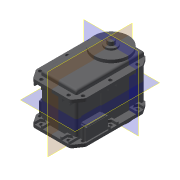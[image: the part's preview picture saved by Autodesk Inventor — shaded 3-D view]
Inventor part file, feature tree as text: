
AUTODESK INVENTOR PART (.ipt)
format: ipt  version: 2020 (Build 240168000, 168)  size: 629,248 bytes
history: native  units: mm
features: other x5, extrude x2, sketch x2
ambient origin geometry x8: Origin, YZ Plane, XZ Plane, XY Plane, X Axis, Y Axis, Z Axis, Center Point
bodies: Body1 (feature_tree)
feature tree (9):
  other  "솔리드1"
  other  "기준1"
  extrude  "돌출1"  Depth=11.0mm
  extrude  "돌출2"  Depth=2.5mm
  other  "작업 평면1"
  other  "작업 평면2"
  other  "작업 평면3"
  sketch  "스케치1"
  sketch  "스케치2"
